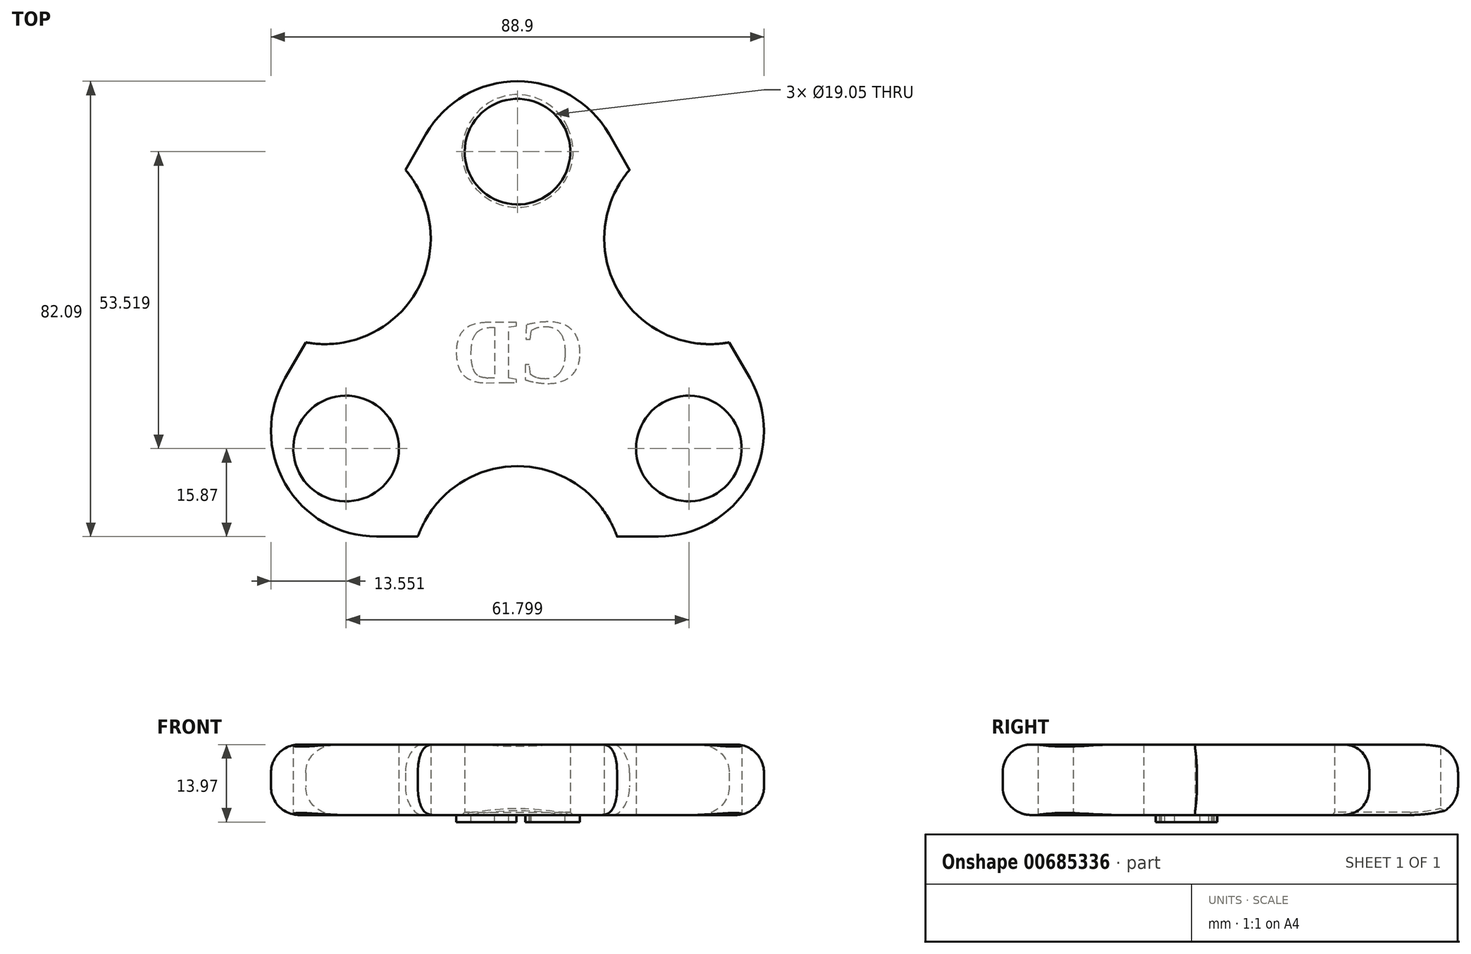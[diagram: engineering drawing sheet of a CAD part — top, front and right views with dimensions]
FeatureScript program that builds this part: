
annotation { "Feature Type Name" : "Feature", "Feature Type Description" : "" }
export const myFeature = defineFeature(function(context is Context, id is Id, definition is map)
    precondition{}
    {
        {
            var Q0;
            Q0=qCreatedBy(makeId("Top.planeOp"),FACE);
            var sketch = newSketch(context, id + "F0", { "sketchPlane" : qUnion([Q0])});
            skCircle(sketch, "E0", {"center": v(0, 29.33) * mm, "radius": 19.05 * mm, "construction": true});
            skLineSegment(sketch, "E1", {"start": v(0, 29.33) * mm, "end": v(-25.4, -14.66) * mm, "construction": true});
            skLineSegment(sketch, "E2", {"start": v(-25.4, -14.66) * mm, "end": v(25.4, -14.66) * mm, "construction": true});
            skLineSegment(sketch, "E3", {"start": v(25.4, -14.66) * mm, "end": v(0, 29.33) * mm, "construction": true});
            skCircle(sketch, "E4", {"center": v(-25.4, -14.66) * mm, "radius": 19.05 * mm, "construction": true});
            skCircle(sketch, "E5", {"center": v(25.4, -14.66) * mm, "radius": 19.05 * mm, "construction": true});
            skLineSegment(sketch, "E6", {"start": v(-16.5, 38.85) * mm, "end": v(-41.9, -5.14) * mm});
            skLineSegment(sketch, "E7", {"start": v(16.5, 38.85) * mm, "end": v(41.9, -5.14) * mm});
            skLineSegment(sketch, "E8", {"start": v(25.4, -33.71) * mm, "end": v(-25.4, -33.71) * mm});
            skArc(sketch, "E9", {"start": v(-16.5, 38.85) * mm, "mid": v(0, 48.38) * mm, "end": v(16.5, 38.85) * mm});
            skArc(sketch, "E10", {"start": v(41.9, -5.14) * mm, "mid": v(41.9, -24.19) * mm, "end": v(25.4, -33.71) * mm});
            skArc(sketch, "E11", {"start": v(-41.9, -5.14) * mm, "mid": v(-41.9, -24.19) * mm, "end": v(-25.4, -33.71) * mm});
            skLineSegment(sketch, "E12", {"start": v(0, 29.33) * mm, "end": v(0, -14.66) * mm, "construction": true});
            skLineSegment(sketch, "E13", {"start": v(-25.4, -14.66) * mm, "end": v(12.7, 7.33) * mm, "construction": true});
            skLineSegment(sketch, "E14", {"start": v(25.4, -14.66) * mm, "end": v(-12.7, 7.33) * mm, "construction": true});
            skSolve(sketch);
        }
        {
            var Q0;
            Q0 = qSketchRegion(id + "F0", true);
            extrude(context, id + "F1", {"entities" : qUnion([Q0]), "depth" : 12.7 * mm, "offsetDistance" : 25.4 * mm});
        }
        {
            var Q0;
            Q0=qCreatedBy(makeId("Top.planeOp"),FACE);
            var sketch = newSketch(context, id + "F2", { "sketchPlane" : qUnion([Q0])});
            skCircle(sketch, "E15", {"center": v(30.9, -17.84) * mm, "radius": 9.53 * mm});
            skCircle(sketch, "E16", {"center": v(-30.9, -17.84) * mm, "radius": 9.53 * mm});
            skCircle(sketch, "E17", {"center": v(0, 35.68) * mm, "radius": 9.53 * mm});
            skLineSegment(sketch, "E18", {"start": v(0, 48.38) * mm, "end": v(0, 0) * mm, "construction": true});
            skLineSegment(sketch, "E19", {"start": v(0, 0) * mm, "end": v(41.9, -24.19) * mm, "construction": true});
            skLineSegment(sketch, "E20", {"start": v(0, 0) * mm, "end": v(-41.9, -24.19) * mm, "construction": true});
            skSolve(sketch);
        }
        {
            var Q0;
            Q0 = qSketchRegion(id + "F2", true);
            var Q1;
            Q1=makeQuery(id+"F1.opExtrude","CAP_FACE",FACE,{"disambiguationData":[OSD([sQuery(id+"F0.wireOp",EDGE,"E6"),sQuery(id+"F0.wireOp",EDGE,"E7"),sQuery(id+"F0.wireOp",EDGE,"E8"),sQuery(id+"F0.wireOp",EDGE,"E9"),sQuery(id+"F0.wireOp",EDGE,"E10"),sQuery(id+"F0.wireOp",EDGE,"E11")])],"isStart":false});
            extrude(context, id + "F3", {"entities" : qUnion([Q0]), "operationType" : NewBodyOperationType.REMOVE, "endBound" : BoundingType.UP_TO_SURFACE, "depth" : 25.4 * mm, "endBoundEntityFace" : qUnion([Q1]), "offsetDistance" : 25.4 * mm});
        }
        {
            var Q0;
            Q0=qCreatedBy(makeId("Top.planeOp"),FACE);
            var sketch = newSketch(context, id + "F4", { "sketchPlane" : qUnion([Q0])});
            skLineSegment(sketch, "E21", {"start": v(0, 29.33) * mm, "end": v(-25.4, -14.66) * mm, "construction": true});
            skLineSegment(sketch, "E22", {"start": v(-25.4, -14.66) * mm, "end": v(25.4, -14.66) * mm, "construction": true});
            skLineSegment(sketch, "E23", {"start": v(25.4, -14.66) * mm, "end": v(0, 29.33) * mm, "construction": true});
            skLineSegment(sketch, "E24", {"start": v(0, 29.33) * mm, "end": v(-34.7, 20.03) * mm, "construction": true});
            skLineSegment(sketch, "E25", {"start": v(-34.7, 20.03) * mm, "end": v(-25.4, -14.66) * mm, "construction": true});
            skCircle(sketch, "E26", {"center": v(-34.7, 20.03) * mm, "radius": 19.05 * mm});
            skLineSegment(sketch, "E27", {"start": v(0, 29.33) * mm, "end": v(34.7, 20.03) * mm, "construction": true});
            skLineSegment(sketch, "E28", {"start": v(34.7, 20.03) * mm, "end": v(25.4, -14.66) * mm, "construction": true});
            skLineSegment(sketch, "E29", {"start": v(25.4, -14.66) * mm, "end": v(0, -40.06) * mm, "construction": true});
            skLineSegment(sketch, "E30", {"start": v(0, -40.06) * mm, "end": v(-25.4, -14.66) * mm, "construction": true});
            skCircle(sketch, "E31", {"center": v(34.7, 20.03) * mm, "radius": 19.05 * mm});
            skCircle(sketch, "E32", {"center": v(0, -40.06) * mm, "radius": 19.05 * mm});
            skSolve(sketch);
        }
        {
            var Q0;
            Q0 = qSketchRegion(id + "F4", true);
            var Q1;
            Q1=makeQuery(id+"F1.opExtrude","CAP_FACE",FACE,{"disambiguationData":[OSD([sQuery(id+"F0.wireOp",EDGE,"E6"),sQuery(id+"F0.wireOp",EDGE,"E7"),sQuery(id+"F0.wireOp",EDGE,"E8"),sQuery(id+"F0.wireOp",EDGE,"E9"),sQuery(id+"F0.wireOp",EDGE,"E10"),sQuery(id+"F0.wireOp",EDGE,"E11")])],"isStart":false});
            extrude(context, id + "F5", {"entities" : qUnion([Q0]), "operationType" : NewBodyOperationType.REMOVE, "endBound" : BoundingType.UP_TO_SURFACE, "depth" : 25.4 * mm, "endBoundEntityFace" : qUnion([Q1]), "offsetDistance" : 25.4 * mm});
        }
        {
            var Q0;
            Q0=makeQuery(id+"F5.boolean.opBoolean","COPY",EDGE,{"derivedFrom":makeQuery(id+"F5.opExtrude","CAP_EDGE",EDGE,{"disambiguationData":[OSD([sQuery(id+"F4.wireOp",EDGE,"E26")])],"isStart":false})});
            var Q1;
            Q1=makeQuery(id+"F1.opExtrude","CAP_EDGE",EDGE,{"disambiguationData":[OSD([sQuery(id+"F0.wireOp",EDGE,"E9")])],"isStart":false});
            var Q2;
            Q2=makeQuery(id+"F5.boolean.opBoolean","COPY",EDGE,{"derivedFrom":makeQuery(id+"F5.opExtrude","CAP_EDGE",EDGE,{"disambiguationData":[OSD([sQuery(id+"F4.wireOp",EDGE,"E31")])],"isStart":false})});
            var Q3;
            Q3=makeQuery(id+"F1.opExtrude","CAP_EDGE",EDGE,{"disambiguationData":[OSD([sQuery(id+"F0.wireOp",EDGE,"E10")])],"isStart":false});
            var Q4;
            Q4=makeQuery(id+"F5.boolean.opBoolean","COPY",EDGE,{"derivedFrom":makeQuery(id+"F5.opExtrude","CAP_EDGE",EDGE,{"disambiguationData":[OSD([sQuery(id+"F4.wireOp",EDGE,"E32")])],"isStart":false})});
            var Q5;
            Q5=makeQuery(id+"F1.opExtrude","CAP_EDGE",EDGE,{"disambiguationData":[OSD([sQuery(id+"F0.wireOp",EDGE,"E11")])],"isStart":false});
            var Q6;
            Q6=makeQuery(id+"F5.boolean.opBoolean","COPY",EDGE,{"derivedFrom":makeQuery(id+"F5.opExtrude","CAP_EDGE",EDGE,{"disambiguationData":[OSD([sQuery(id+"F4.wireOp",EDGE,"E32")])],"isStart":true})});
            var Q7;
            Q7=makeQuery(id+"F1.opExtrude","CAP_EDGE",EDGE,{"disambiguationData":[OSD([sQuery(id+"F0.wireOp",EDGE,"E11")])],"isStart":true});
            var Q8;
            Q8=makeQuery(id+"F5.boolean.opBoolean","COPY",EDGE,{"derivedFrom":makeQuery(id+"F5.opExtrude","CAP_EDGE",EDGE,{"disambiguationData":[OSD([sQuery(id+"F4.wireOp",EDGE,"E26")])],"isStart":true})});
            var Q9;
            Q9=makeQuery(id+"F1.opExtrude","CAP_EDGE",EDGE,{"disambiguationData":[OSD([sQuery(id+"F0.wireOp",EDGE,"E9")])],"isStart":true});
            var Q10;
            Q10=makeQuery(id+"F5.boolean.opBoolean","COPY",EDGE,{"derivedFrom":makeQuery(id+"F5.opExtrude","CAP_EDGE",EDGE,{"disambiguationData":[OSD([sQuery(id+"F4.wireOp",EDGE,"E31")])],"isStart":true})});
            var Q11;
            Q11=makeQuery(id+"F1.opExtrude","CAP_EDGE",EDGE,{"disambiguationData":[OSD([sQuery(id+"F0.wireOp",EDGE,"E10")])],"isStart":true});
            fillet(context, id + "F6", {"entities" : qUnion([Q0, Q1, Q2, Q3, Q4, Q5, Q6, Q7, Q8, Q9, Q10, Q11]), "radius" : 5.08 * mm, "tangentPropagation" : true, "allowEdgeOverflow" : false});
        }
        {
            var Q0;
            Q0=makeQuery(id+"F6.opFillet","BLEND_EDGE",EDGE,{"blendedFrom":[makeQuery(id+"F1.opExtrude","CAP_EDGE",EDGE,{"disambiguationData":[OSD([sQuery(id+"F0.wireOp",EDGE,"E9")])],"isStart":true}),makeQuery(id+"F3.boolean.opBoolean","COPY",FACE,{"derivedFrom":makeQuery(id+"F3.opExtrude","SWEPT_FACE",FACE,{"disambiguationData":[OSD([sQuery(id+"F2.wireOp",EDGE,"E17")])]})})],"blendedInto":[makeQuery(id+"F3.boolean.opBoolean","COPY",FACE,{"derivedFrom":makeQuery(id+"F3.opExtrude","SWEPT_FACE",FACE,{"disambiguationData":[OSD([sQuery(id+"F2.wireOp",EDGE,"E17")])]})})]});
            var Q1;
            Q1=makeQuery(id+"F3.boolean.opBoolean","COPY",EDGE,{"derivedFrom":makeQuery(id+"F3.opExtrude","CAP_EDGE",EDGE,{"disambiguationData":[OSD([sQuery(id+"F2.wireOp",EDGE,"E16")])],"isStart":true})});
            var Q2;
            Q2=makeQuery(id+"F3.boolean.opBoolean","COPY",EDGE,{"derivedFrom":makeQuery(id+"F3.opExtrude","CAP_EDGE",EDGE,{"disambiguationData":[OSD([sQuery(id+"F2.wireOp",EDGE,"E15")])],"isStart":true})});
            var Q3;
            Q3=makeQuery(id+"F3.boolean.opBoolean","COPY",EDGE,{"derivedFrom":makeQuery(id+"F3.opExtrude","CAP_EDGE",EDGE,{"disambiguationData":[OSD([sQuery(id+"F2.wireOp",EDGE,"E15")])],"isStart":false})});
            var Q4;
            Q4=makeQuery(id+"F3.boolean.opBoolean","COPY",EDGE,{"derivedFrom":makeQuery(id+"F3.opExtrude","CAP_EDGE",EDGE,{"disambiguationData":[OSD([sQuery(id+"F2.wireOp",EDGE,"E16")])],"isStart":false})});
            var Q5;
            Q5=makeQuery(id+"F3.boolean.opBoolean","COPY",EDGE,{"derivedFrom":makeQuery(id+"F3.opExtrude","CAP_EDGE",EDGE,{"disambiguationData":[OSD([sQuery(id+"F2.wireOp",EDGE,"E17")])],"isStart":false})});
            chamfer(context, id + "F7", {"entities" : qUnion([Q0, Q1, Q2, Q3, Q4, Q5]), "width" : 0.5 * mm, "tangentPropagation" : true});
        }
        {
            var Q0;
            Q0=makeQuery(id+"F1.opExtrude","CAP_FACE",FACE,{"disambiguationData":[OSD([sQuery(id+"F0.wireOp",EDGE,"E6"),sQuery(id+"F0.wireOp",EDGE,"E7"),sQuery(id+"F0.wireOp",EDGE,"E8"),sQuery(id+"F0.wireOp",EDGE,"E9"),sQuery(id+"F0.wireOp",EDGE,"E10"),sQuery(id+"F0.wireOp",EDGE,"E11")])],"isStart":true});
            var sketch = newSketch(context, id + "F8", { "sketchPlane" : qUnion([Q0])});
            skLineSegment(sketch, "E33", {"start": v(0, -35.68) * mm, "end": v(30.9, 17.84) * mm, "construction": true});
            skLineSegment(sketch, "E34", {"start": v(30.9, 17.84) * mm, "end": v(-30.9, 17.84) * mm, "construction": true});
            skLineSegment(sketch, "E35", {"start": v(-30.9, 17.84) * mm, "end": v(0, -35.68) * mm, "construction": true});
            skPoint(sketch, "E36", {"position": v(0, 15.93) * mm});
            skText(sketch, "E37", { "text": "CD", "fontName": "Tinos-Bold.ttf"});
            skPoint(sketch, "E38", {"position": v(0, 0) * mm});
            const initialGuessF8  = {"E37": [0.01207, 0.00596, -1, 0, 0.01192]};
            skSetInitialGuess(sketch, initialGuessF8);
            skSolve(sketch);
        }
        {
            var Q0;
            Q0 = qSketchRegion(id + "F8", true);
            extrude(context, id + "F9", {"entities" : qUnion([Q0]), "operationType" : NewBodyOperationType.ADD, "depth" : 1.27 * mm, "offsetDistance" : 25.4 * mm});
        }
    });
